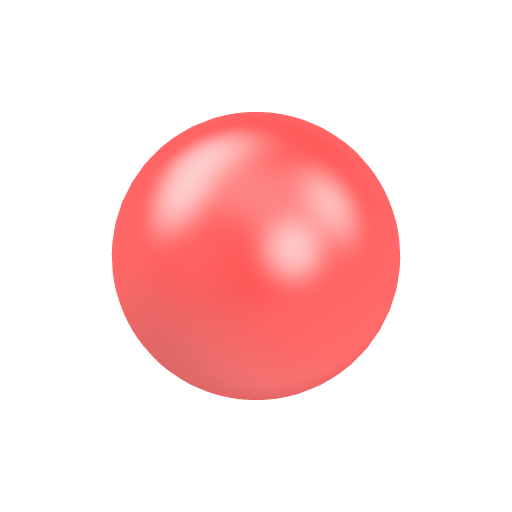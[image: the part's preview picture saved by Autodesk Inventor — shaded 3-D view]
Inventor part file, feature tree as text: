
AUTODESK INVENTOR PART (.ipt)
format: ipt  version: 2023 (Build 270158000, 158)  size: 144,384 bytes
history: native  units: in
note: dims shown in document units (in); Inventor stores cm internally (conversion verified against a paired STEP export)
features: revolve x1, sketch x1
ambient origin geometry x8: Origin, YZ Plane, XZ Plane, XY Plane, X Axis, Y Axis, Z Axis, Center Point
bodies: Solid1 (feature_tree)
feature tree (2):
  revolve  "Revolution1"  Angle=90.0deg
  sketch  "Sketch1"  dims[d0=3.0in d1=90.0deg]
